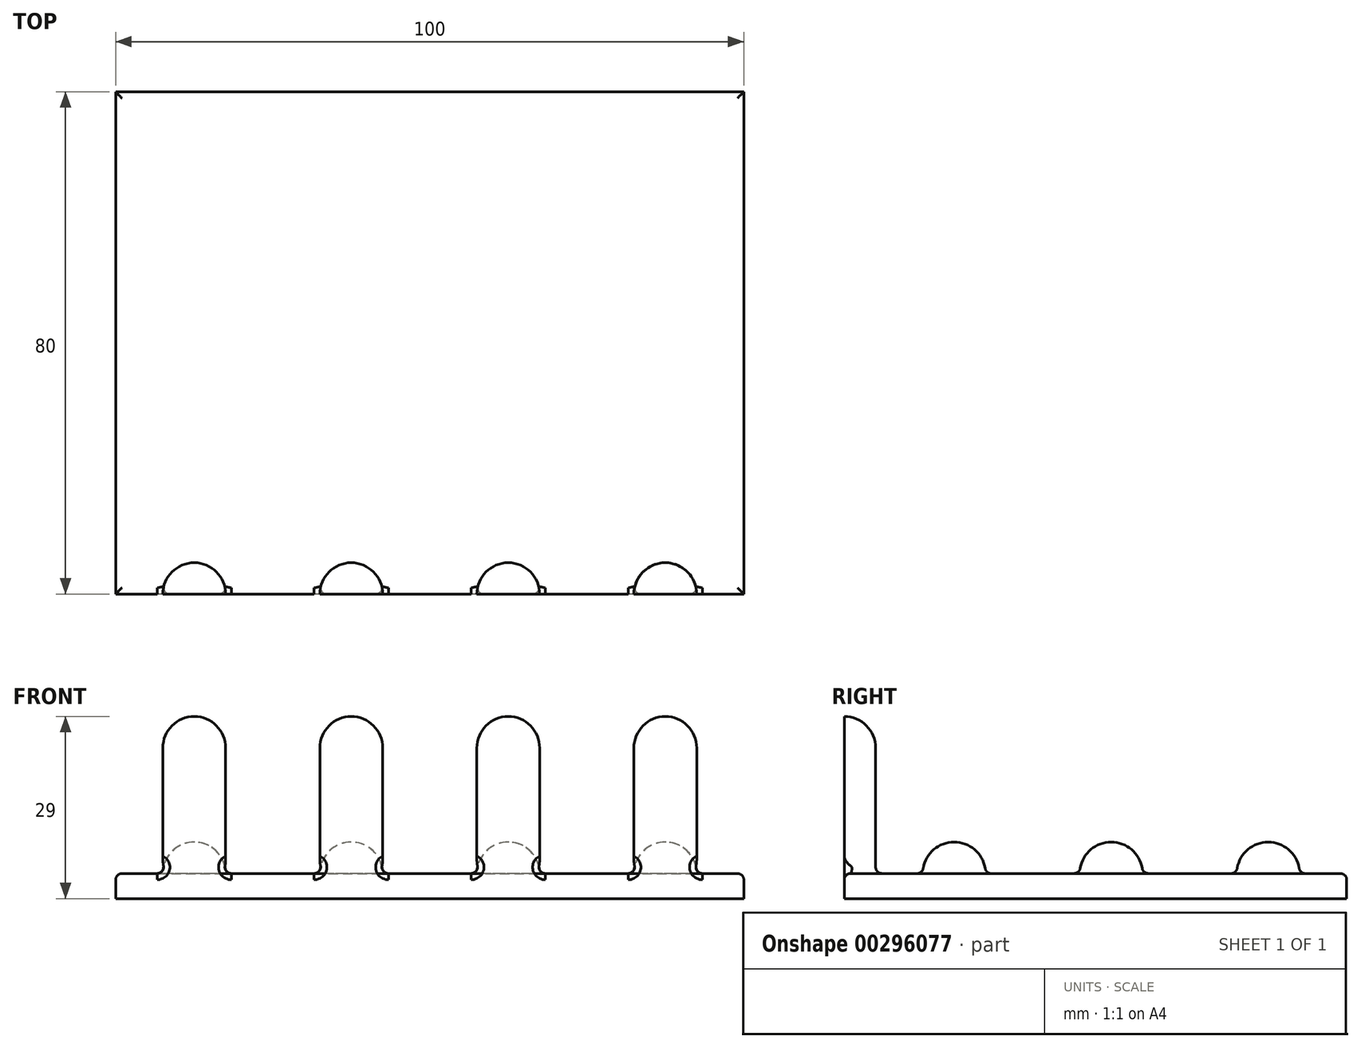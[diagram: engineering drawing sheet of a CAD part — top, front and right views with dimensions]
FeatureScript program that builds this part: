
annotation { "Feature Type Name" : "Feature", "Feature Type Description" : "" }
export const myFeature = defineFeature(function(context is Context, id is Id, definition is map)
    precondition{}
    {
        {
            var Q0;
            Q0=qCreatedBy(makeId("Top.planeOp"),FACE);
            var sketch = newSketch(context, id + "F0", { "sketchPlane" : qUnion([Q0])});
            skLineSegment(sketch, "E0.bottom", {"start": v(50, 37.5) * mm, "end": v(-50, 37.5) * mm});
            skLineSegment(sketch, "E0.top", {"start": v(50, -37.5) * mm, "end": v(-50, -37.5) * mm});
            skLineSegment(sketch, "E0.left", {"start": v(50, 37.5) * mm, "end": v(50, -37.5) * mm});
            skLineSegment(sketch, "E0.right", {"start": v(-50, 37.5) * mm, "end": v(-50, -37.5) * mm});
            skPoint(sketch, "E0.middle", {"position": v(0, 0) * mm});
            skSolve(sketch);
        }
        {
            var Q0;
            Q0=makeQuery(id+"F0.imprint","IMPRINT",FACE,{"disambiguationData":[TD([[makeQuery(id+"F0.imprint","IMPRINT",EDGE,{"derivedFrom":sQuery(id+"F0.wireOp",EDGE,"E0.bottom")}),1.0]])]});
            extrude(context, id + "F1", {"entities" : qUnion([Q0]), "depth" : 4 * mm});
        }
        {
            var Q0;
            Q0=makeQuery(id+"F1.opExtrude","CAP_FACE",FACE,{"disambiguationData":[OSD([sQuery(id+"F0.wireOp",EDGE,"E0.bottom"),sQuery(id+"F0.wireOp",EDGE,"E0.top"),sQuery(id+"F0.wireOp",EDGE,"E0.left"),sQuery(id+"F0.wireOp",EDGE,"E0.right")])],"isStart":false});
            var sketch = newSketch(context, id + "F2", { "sketchPlane" : qUnion([Q0])});
            skCircle(sketch, "E1", {"center": v(-37.5, -25) * mm, "radius": 5 * mm});
            skCircle(sketch, "E2.0.1.0", {"center": v(-37.5, 0) * mm, "radius": 5 * mm});
            skCircle(sketch, "E2.0.2.0", {"center": v(-37.5, 25) * mm, "radius": 5 * mm});
            skCircle(sketch, "E2.1.0.0", {"center": v(-12.5, -25) * mm, "radius": 5 * mm});
            skCircle(sketch, "E2.1.1.0", {"center": v(-12.5, 0) * mm, "radius": 5 * mm});
            skCircle(sketch, "E2.1.2.0", {"center": v(-12.5, 25) * mm, "radius": 5 * mm});
            skCircle(sketch, "E2.2.0.0", {"center": v(12.5, -25) * mm, "radius": 5 * mm});
            skCircle(sketch, "E2.2.1.0", {"center": v(12.5, 0) * mm, "radius": 5 * mm});
            skCircle(sketch, "E2.2.2.0", {"center": v(12.5, 25) * mm, "radius": 5 * mm});
            skCircle(sketch, "E2.3.0.0", {"center": v(37.5, -25) * mm, "radius": 5 * mm});
            skCircle(sketch, "E2.3.1.0", {"center": v(37.5, 0) * mm, "radius": 5 * mm});
            skCircle(sketch, "E2.3.2.0", {"center": v(37.5, 25) * mm, "radius": 5 * mm});
            skLineSegment(sketch, "E2.direction1", {"start": v(-37.5, -25) * mm, "end": v(-12.5, -25) * mm, "construction": true});
            skLineSegment(sketch, "E2.direction2", {"start": v(-37.5, -25) * mm, "end": v(-37.5, 0) * mm, "construction": true});
            skSolve(sketch);
        }
        {
            var Q0;
            Q0=makeQuery(id+"F2.imprint","IMPRINT",FACE,{"disambiguationData":[TD([[makeQuery(id+"F2.imprint","IMPRINT",EDGE,{"derivedFrom":sQuery(id+"F2.wireOp",EDGE,"E1")}),1.0]])]});
            var Q1;
            Q1=makeQuery(id+"F2.imprint","IMPRINT",FACE,{"disambiguationData":[TD([[makeQuery(id+"F2.imprint","IMPRINT",EDGE,{"derivedFrom":sQuery(id+"F2.wireOp",EDGE,"E2.1.0.0")}),1.0]])]});
            var Q2;
            Q2=makeQuery(id+"F2.imprint","IMPRINT",FACE,{"disambiguationData":[TD([[makeQuery(id+"F2.imprint","IMPRINT",EDGE,{"derivedFrom":sQuery(id+"F2.wireOp",EDGE,"E2.1.1.0")}),1.0]])]});
            var Q3;
            Q3=makeQuery(id+"F2.imprint","IMPRINT",FACE,{"disambiguationData":[TD([[makeQuery(id+"F2.imprint","IMPRINT",EDGE,{"derivedFrom":sQuery(id+"F2.wireOp",EDGE,"E2.0.1.0")}),1.0]])]});
            var Q4;
            Q4=makeQuery(id+"F2.imprint","IMPRINT",FACE,{"disambiguationData":[TD([[makeQuery(id+"F2.imprint","IMPRINT",EDGE,{"derivedFrom":sQuery(id+"F2.wireOp",EDGE,"E2.0.2.0")}),1.0]])]});
            var Q5;
            Q5=makeQuery(id+"F2.imprint","IMPRINT",FACE,{"disambiguationData":[TD([[makeQuery(id+"F2.imprint","IMPRINT",EDGE,{"derivedFrom":sQuery(id+"F2.wireOp",EDGE,"E2.1.2.0")}),1.0]])]});
            var Q6;
            Q6=makeQuery(id+"F2.imprint","IMPRINT",FACE,{"disambiguationData":[TD([[makeQuery(id+"F2.imprint","IMPRINT",EDGE,{"derivedFrom":sQuery(id+"F2.wireOp",EDGE,"E2.2.2.0")}),1.0]])]});
            var Q7;
            Q7=makeQuery(id+"F2.imprint","IMPRINT",FACE,{"disambiguationData":[TD([[makeQuery(id+"F2.imprint","IMPRINT",EDGE,{"derivedFrom":sQuery(id+"F2.wireOp",EDGE,"E2.3.2.0")}),1.0]])]});
            var Q8;
            Q8=makeQuery(id+"F2.imprint","IMPRINT",FACE,{"disambiguationData":[TD([[makeQuery(id+"F2.imprint","IMPRINT",EDGE,{"derivedFrom":sQuery(id+"F2.wireOp",EDGE,"E2.2.1.0")}),1.0]])]});
            var Q9;
            Q9=makeQuery(id+"F2.imprint","IMPRINT",FACE,{"disambiguationData":[TD([[makeQuery(id+"F2.imprint","IMPRINT",EDGE,{"derivedFrom":sQuery(id+"F2.wireOp",EDGE,"E2.2.0.0")}),1.0]])]});
            var Q10;
            Q10=makeQuery(id+"F2.imprint","IMPRINT",FACE,{"disambiguationData":[TD([[makeQuery(id+"F2.imprint","IMPRINT",EDGE,{"derivedFrom":sQuery(id+"F2.wireOp",EDGE,"E2.3.0.0")}),1.0]])]});
            var Q11;
            Q11=makeQuery(id+"F2.imprint","IMPRINT",FACE,{"disambiguationData":[TD([[makeQuery(id+"F2.imprint","IMPRINT",EDGE,{"derivedFrom":sQuery(id+"F2.wireOp",EDGE,"E2.3.1.0")}),1.0]])]});
            extrude(context, id + "F3", {"entities" : qUnion([Q0, Q1, Q2, Q3, Q4, Q5, Q6, Q7, Q8, Q9, Q10, Q11]), "operationType" : NewBodyOperationType.ADD, "depth" : 5 * mm});
        }
        {
            var Q0;
            Q0=makeQuery(id+"F3.opExtrude","CAP_EDGE",EDGE,{"disambiguationData":[OSD([sQuery(id+"F2.wireOp",EDGE,"E1")])],"isStart":false});
            var Q1;
            Q1=makeQuery(id+"F3.opExtrude","CAP_EDGE",EDGE,{"disambiguationData":[OSD([sQuery(id+"F2.wireOp",EDGE,"E2.0.1.0")])],"isStart":false});
            var Q2;
            Q2=makeQuery(id+"F3.opExtrude","CAP_EDGE",EDGE,{"disambiguationData":[OSD([sQuery(id+"F2.wireOp",EDGE,"E2.0.2.0")])],"isStart":false});
            var Q3;
            Q3=makeQuery(id+"F3.opExtrude","CAP_EDGE",EDGE,{"disambiguationData":[OSD([sQuery(id+"F2.wireOp",EDGE,"E2.1.2.0")])],"isStart":false});
            var Q4;
            Q4=makeQuery(id+"F3.opExtrude","CAP_EDGE",EDGE,{"disambiguationData":[OSD([sQuery(id+"F2.wireOp",EDGE,"E2.1.1.0")])],"isStart":false});
            var Q5;
            Q5=makeQuery(id+"F3.opExtrude","CAP_EDGE",EDGE,{"disambiguationData":[OSD([sQuery(id+"F2.wireOp",EDGE,"E2.1.0.0")])],"isStart":false});
            var Q6;
            Q6=makeQuery(id+"F3.opExtrude","CAP_EDGE",EDGE,{"disambiguationData":[OSD([sQuery(id+"F2.wireOp",EDGE,"E2.2.0.0")])],"isStart":false});
            var Q7;
            Q7=makeQuery(id+"F3.opExtrude","CAP_EDGE",EDGE,{"disambiguationData":[OSD([sQuery(id+"F2.wireOp",EDGE,"E2.2.1.0")])],"isStart":false});
            var Q8;
            Q8=makeQuery(id+"F3.opExtrude","CAP_EDGE",EDGE,{"disambiguationData":[OSD([sQuery(id+"F2.wireOp",EDGE,"E2.2.2.0")])],"isStart":false});
            var Q9;
            Q9=makeQuery(id+"F3.opExtrude","CAP_EDGE",EDGE,{"disambiguationData":[OSD([sQuery(id+"F2.wireOp",EDGE,"E2.3.2.0")])],"isStart":false});
            var Q10;
            Q10=makeQuery(id+"F3.opExtrude","CAP_EDGE",EDGE,{"disambiguationData":[OSD([sQuery(id+"F2.wireOp",EDGE,"E2.3.1.0")])],"isStart":false});
            var Q11;
            Q11=makeQuery(id+"F3.opExtrude","CAP_EDGE",EDGE,{"disambiguationData":[OSD([sQuery(id+"F2.wireOp",EDGE,"E2.3.0.0")])],"isStart":false});
            fillet(context, id + "F4", {"entities" : qUnion([Q0, Q1, Q2, Q3, Q4, Q5, Q6, Q7, Q8, Q9, Q10, Q11]), "radius" : 5 * mm, "tangentPropagation" : true, "allowEdgeOverflow" : false});
        }
        {
            var Q0;
            Q0=makeQuery(id+"F1.opExtrude","SWEPT_FACE",FACE,{"disambiguationData":[OSD([sQuery(id+"F0.wireOp",EDGE,"E0.top")])]});
            extrude(context, id + "F5", {"entities" : qUnion([Q0]), "operationType" : NewBodyOperationType.ADD, "depth" : 5 * mm});
        }
        {
            var Q0;
            {var subQ0=sQuery(id+"F0.wireOp",EDGE,"E0.top");Q0=makeQuery(id+"F5.boolean.opBoolean","MERGE",FACE,{"derivedFrom":[makeQuery(id+"F1.opExtrude","CAP_FACE",FACE,{"disambiguationData":[OSD([sQuery(id+"F0.wireOp",EDGE,"E0.bottom"),subQ0,sQuery(id+"F0.wireOp",EDGE,"E0.left"),sQuery(id+"F0.wireOp",EDGE,"E0.right")])],"isStart":false}),makeQuery(id+"F5.opExtrude","SWEPT_FACE",FACE,{"disambiguationData":[OSD([subQ0]),TDD([makeQuery(id+"F1.opExtrude","CAP_EDGE",EDGE,{"disambiguationData":[OSD([subQ0])],"isStart":false})])]})]});}
            var sketch = newSketch(context, id + "F6", { "sketchPlane" : qUnion([Q0])});
            skArc(sketch, "E3", {"start": v(-32.5, -42.5) * mm, "mid": v(-37.5, -37.5) * mm, "end": v(-42.5, -42.5) * mm});
            skArc(sketch, "E4.1.0.0", {"start": v(-7.5, -42.5) * mm, "mid": v(-12.5, -37.5) * mm, "end": v(-17.5, -42.5) * mm});
            skArc(sketch, "E4.2.0.0", {"start": v(17.5, -42.5) * mm, "mid": v(12.5, -37.5) * mm, "end": v(7.5, -42.5) * mm});
            skArc(sketch, "E4.3.0.0", {"start": v(42.5, -42.5) * mm, "mid": v(37.5, -37.5) * mm, "end": v(32.5, -42.5) * mm});
            skLineSegment(sketch, "E4.direction1", {"start": v(-42.5, -42.5) * mm, "end": v(-17.5, -42.5) * mm, "construction": true});
            skSolve(sketch);
        }
        {
            var Q0;
            {var subQ0=sQuery(id+"F6.wireOp",EDGE,"E3");Q0=makeQuery(id+"F6.imprint","IMPRINT",FACE,{"disambiguationData":[TD([[makeQuery(id+"F6.imprint","IMPRINT",EDGE,{"derivedFrom":subQ0}),1.0]])]});}
            var Q1;
            {var subQ0=sQuery(id+"F6.wireOp",EDGE,"E4.1.0.0");Q1=makeQuery(id+"F6.imprint","IMPRINT",FACE,{"disambiguationData":[TD([[makeQuery(id+"F6.imprint","IMPRINT",EDGE,{"derivedFrom":subQ0}),1.0]])]});}
            var Q2;
            {var subQ0=sQuery(id+"F6.wireOp",EDGE,"E4.2.0.0");Q2=makeQuery(id+"F6.imprint","IMPRINT",FACE,{"disambiguationData":[TD([[makeQuery(id+"F6.imprint","IMPRINT",EDGE,{"derivedFrom":subQ0}),1.0]])]});}
            var Q3;
            {var subQ0=sQuery(id+"F6.wireOp",EDGE,"E4.3.0.0");Q3=makeQuery(id+"F6.imprint","IMPRINT",FACE,{"disambiguationData":[TD([[makeQuery(id+"F6.imprint","IMPRINT",EDGE,{"derivedFrom":subQ0}),1.0]])]});}
            extrude(context, id + "F7", {"entities" : qUnion([Q0, Q1, Q2, Q3]), "operationType" : NewBodyOperationType.ADD, "depth" : 25 * mm});
        }
        {
            var Q0;
            Q0=makeQuery(id+"F7.opExtrude","CAP_EDGE",EDGE,{"disambiguationData":[OSD([sQuery(id+"F6.wireOp",EDGE,"E3")])],"isStart":false});
            var Q1;
            Q1=makeQuery(id+"F7.opExtrude","CAP_EDGE",EDGE,{"disambiguationData":[OSD([sQuery(id+"F6.wireOp",EDGE,"E4.1.0.0")])],"isStart":false});
            var Q2;
            Q2=makeQuery(id+"F7.opExtrude","CAP_EDGE",EDGE,{"disambiguationData":[OSD([sQuery(id+"F6.wireOp",EDGE,"E4.2.0.0")])],"isStart":false});
            var Q3;
            Q3=makeQuery(id+"F7.opExtrude","CAP_EDGE",EDGE,{"disambiguationData":[OSD([sQuery(id+"F6.wireOp",EDGE,"E4.3.0.0")])],"isStart":false});
            fillet(context, id + "F8", {"entities" : qUnion([Q0, Q1, Q2, Q3]), "radius" : 5 * mm, "tangentPropagation" : true, "allowEdgeOverflow" : false});
        }
        {
            var Q0;
            {var subQ0=sQuery(id+"F0.wireOp",EDGE,"E0.top");Q0=makeQuery(id+"F5.boolean.opBoolean","MERGE",FACE,{"derivedFrom":[makeQuery(id+"F1.opExtrude","CAP_FACE",FACE,{"disambiguationData":[OSD([sQuery(id+"F0.wireOp",EDGE,"E0.bottom"),subQ0,sQuery(id+"F0.wireOp",EDGE,"E0.left"),sQuery(id+"F0.wireOp",EDGE,"E0.right")])],"isStart":false}),makeQuery(id+"F5.opExtrude","SWEPT_FACE",FACE,{"disambiguationData":[OSD([subQ0]),TDD([makeQuery(id+"F1.opExtrude","CAP_EDGE",EDGE,{"disambiguationData":[OSD([subQ0])],"isStart":false})])]})]});}
            fillet(context, id + "F9", {"entities" : qUnion([Q0]), "radius" : 1 * mm, "tangentPropagation" : true, "allowEdgeOverflow" : false});
        }
    });
